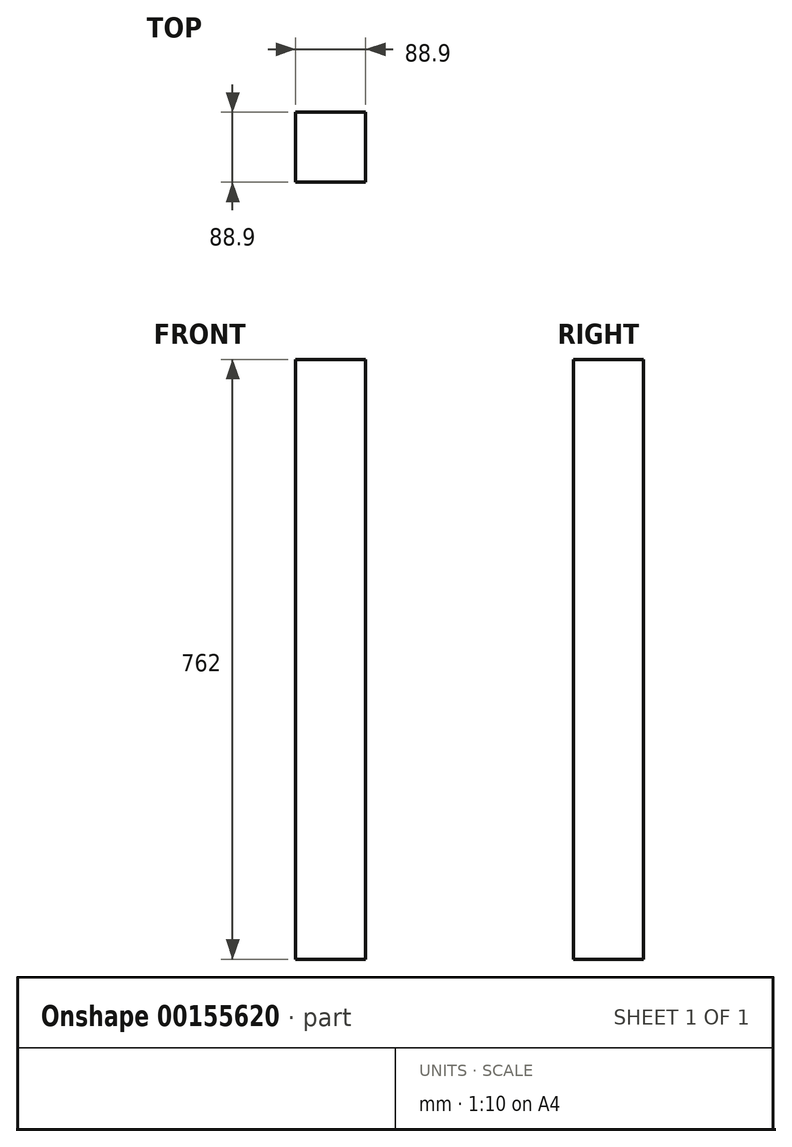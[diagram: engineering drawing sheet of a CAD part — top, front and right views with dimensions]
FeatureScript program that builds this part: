
annotation { "Feature Type Name" : "Feature", "Feature Type Description" : "" }
export const myFeature = defineFeature(function(context is Context, id is Id, definition is map)
    precondition{}
    {
        {
            var Q0;
            Q0=qCreatedBy(makeId("Top.planeOp"),FACE);
            var sketch = newSketch(context, id + "F0", { "sketchPlane" : qUnion([Q0])});
            skLineSegment(sketch, "E0.bottom", {"start": v(-44.45, 44.45) * mm, "end": v(44.45, 44.45) * mm});
            skLineSegment(sketch, "E0.top", {"start": v(-44.45, -44.45) * mm, "end": v(44.45, -44.45) * mm});
            skLineSegment(sketch, "E0.left", {"start": v(-44.45, 44.45) * mm, "end": v(-44.45, -44.45) * mm});
            skLineSegment(sketch, "E0.right", {"start": v(44.45, 44.45) * mm, "end": v(44.45, -44.45) * mm});
            skPoint(sketch, "E0.middle", {"position": v(0, 0) * mm});
            skSolve(sketch);
        }
        {
            var Q0;
            Q0=makeQuery(id+"F0.imprint","IMPRINT",FACE,{"disambiguationData":[TD([[makeQuery(id+"F0.imprint","IMPRINT",EDGE,{"derivedFrom":sQuery(id+"F0.wireOp",EDGE,"E0.bottom")}),-1.0]])]});
            extrude(context, id + "F1", {"entities" : qUnion([Q0]), "depth" : 762 * mm});
        }
    });
